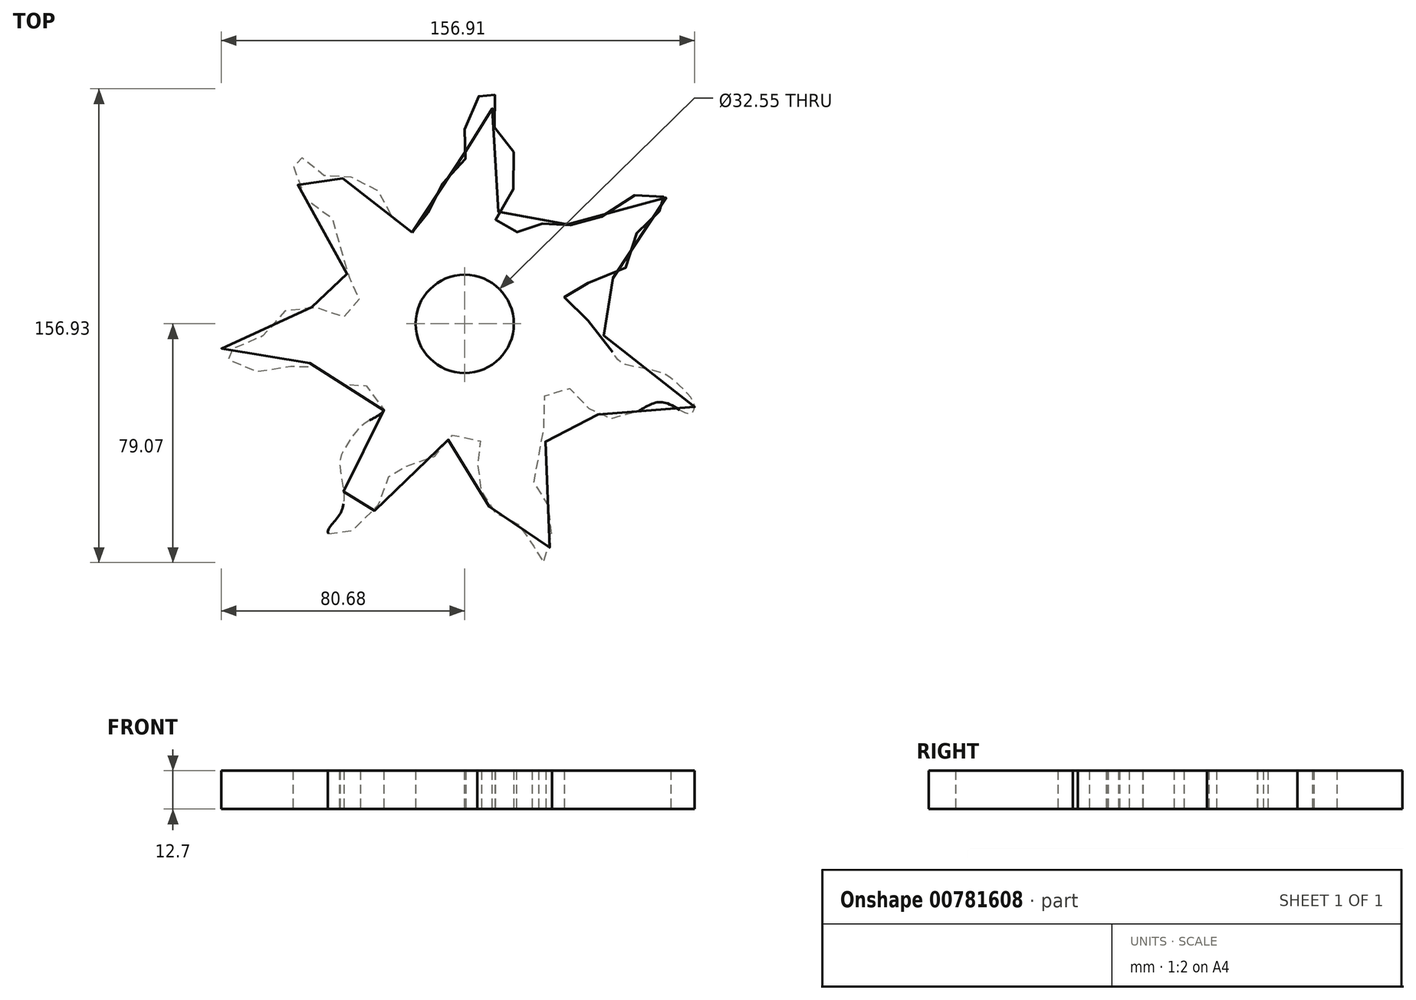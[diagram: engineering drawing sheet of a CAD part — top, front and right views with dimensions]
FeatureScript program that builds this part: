
annotation { "Feature Type Name" : "Feature", "Feature Type Description" : "" }
export const myFeature = defineFeature(function(context is Context, id is Id, definition is map)
    precondition{}
    {
        {
            var Q0;
            Q0=qCreatedBy(makeId("Top.planeOp"),FACE);
            var sketch = newSketch(context, id + "F0", { "sketchPlane" : qUnion([Q0])});
            skFitSpline(sketch, "E0", {"points": [v(-17.38, 30.3) * mm, v(-21.49, 30.3) * mm, v(-24.01, 35.98) * mm, v(-26.85, 41.66) * mm, v(-31.27, 46.4) * mm, v(-36.95, 48.6) * mm, v(-42.53, 48.05) * mm, v(-46.88, 49.16) * mm, v(-51.01, 51.5) * mm, v(-54.8, 55.86) * mm, v(-56.48, 55.97) * mm, v(-56.81, 52.96) * mm, v(-55.7, 47.04) * mm, v(-51.01, 39.46) * mm, v(-45.1, 35.77) * mm, v(-41.53, 31.98) * mm, v(-41.53, 26.4) * mm, v(-40.08, 18.37) * mm, v(-36.28, 13.23) * mm, v(-34.56, 10.82) * mm, v(-36.3, 4.66) * mm, v(-38.03, 2.3) * mm, v(-43.4, 3.24) * mm, v(-47.97, 5.14) * mm, v(-53.65, 5.45) * mm, v(-60.44, 3.72) * mm, v(-65.33, -2.28) * mm, v(-70.22, -6.38) * mm, v(-77.64, -8.28) * mm, v(-80.64, -8.28) * mm, v(-78.43, -11.75) * mm, v(-73.06, -14.9) * mm, v(-66.12, -15.85) * mm, v(-58.55, -14.43) * mm, v(-53.65, -12.7) * mm, v(-49.55, -13.96) * mm, v(-44.66, -18.38) * mm, v(-37.56, -20.27) * mm, v(-34.22, -19.93) * mm, v(-32.21, -20.83) * mm, v(-27.53, -26.63) * mm, v(-27.08, -29.08) * mm, v(-32.66, -32.65) * mm, v(-36.9, -36.9) * mm, v(-40.03, -41.8) * mm, v(-41.36, -45.82) * mm, v(-40.47, -53.4) * mm, v(-40.03, -58.1) * mm, v(-41.36, -63) * mm, v(-44.94, -67.7) * mm, v(-45.16, -69.48) * mm, v(-42.03, -70.15) * mm, v(-32.44, -65.02) * mm, v(-26.63, -55.42) * mm, v(-24.63, -49.62) * mm, v(-21.72, -47.6) * mm, v(-16.15, -46.71) * mm, v(-7.22, -41.36) * mm, v(-3.65, -36.67) * mm, v(4.83, -38.23) * mm, v(5.06, -42.92) * mm, v(4.16, -48.28) * mm, v(5.5, -55.42) * mm, v(8.4, -61) * mm, v(13.54, -64.57) * mm, v(19.34, -67.47) * mm, v(22.92, -73.84) * mm, v(24.52, -77.95) * mm, v(26.1, -79.02) * mm, v(28.63, -71.45) * mm, v(28.63, -63.89) * mm, v(25.44, -55.26) * mm, v(22.53, -51.68) * mm, v(23.85, -45.44) * mm, v(26.9, -36.95) * mm, v(24.52, -28.46) * mm, v(32.16, -19.64) * mm, v(36.93, -24.42) * mm, v(41.71, -28.4) * mm, v(46.49, -31.06) * mm, v(53.92, -30.53) * mm, v(60.82, -27.08) * mm, v(66.92, -26.28) * mm, v(74.62, -29.73) * mm, v(76.21, -27.08) * mm, v(72.5, -21.77) * mm, v(65.07, -16.2) * mm, v(52.86, -13.27) * mm, v(48.88, -9.03) * mm, v(42.77, 0) * mm, v(35.87, 3.18) * mm, v(33.22, 10.35) * mm, v(38, 13.8) * mm, v(44.37, 13.27) * mm, v(54.72, 20.43) * mm, v(56.3, 27.86) * mm, v(60.62, 35.56) * mm, v(64.94, 37.43) * mm, v(68.32, 40.44) * mm, v(66.44, 41.94) * mm, v(62.69, 42.88) * mm, v(56.5, 42.69) * mm, v(48.05, 38.18) * mm, v(40.73, 32) * mm, v(34.35, 32.93) * mm, v(29.66, 33.3) * mm, v(24.6, 32.74) * mm, v(19.71, 29.74) * mm, v(15.96, 31.24) * mm, v(12.2, 32.93) * mm, v(10.14, 35) * mm, v(14.6, 41.63) * mm, v(17.06, 50.56) * mm, v(15.5, 58.37) * mm, v(11.48, 62.61) * mm, v(9.03, 68.86) * mm, v(9.92, 75.56) * mm, v(9.7, 77.56) * mm, v(7.47, 77.56) * mm, v(2.33, 72.2) * mm, v(0, 64.62) * mm, v(0, 61.05) * mm, v(0, 53.9) * mm, v(-4.59, 48.77) * mm, v(-9.72, 43.64) * mm, v(-12.17, 37.17) * mm, v(-13.74, 32.04) * mm, v(-17.38, 30.3) * mm]});
            skCircle(sketch, "E1", {"center": v(0, 0) * mm, "radius": 16.28 * mm});
            skCircle(sketch, "E2", {"center": v(0, 0) * mm, "radius": 13.1 * mm});
            skSolve(sketch);
        }
        {
            var Q0;
            Q0 = qSketchRegion(id + "F0", true);
            extrude(context, id + "F1", {"entities" : qUnion([Q0]), "depth" : 12.7 * mm, "offsetDistance" : 25.4 * mm, "hasSecondDirection" : true, "secondDirectionOppositeDirection" : true, "secondDirectionDepth" : 0 * mm});
        }
    });
